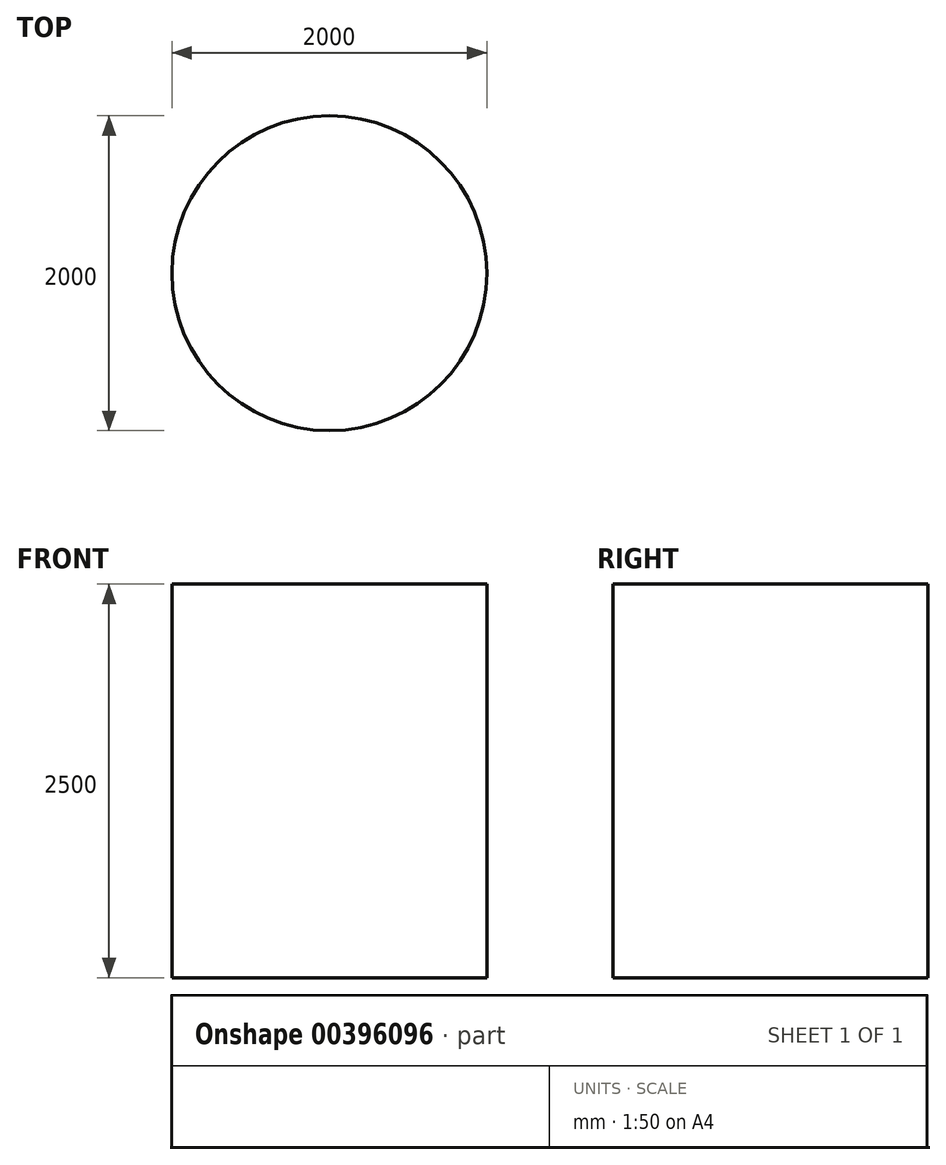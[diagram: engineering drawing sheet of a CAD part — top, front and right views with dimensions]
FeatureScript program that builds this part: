
annotation { "Feature Type Name" : "Feature", "Feature Type Description" : "" }
export const myFeature = defineFeature(function(context is Context, id is Id, definition is map)
    precondition{}
    {
        {
            var Q0;
            Q0=qCreatedBy(makeId("Top.planeOp"),FACE);
            var sketch = newSketch(context, id + "F0", { "sketchPlane" : qUnion([Q0])});
            skCircle(sketch, "E0", {"center": v(0, 0) * mm, "radius": 1000 * mm});
            skSolve(sketch);
        }
        {
            var Q0;
            Q0 = qSketchRegion(id + "F0", true);
            extrude(context, id + "F1", {"entities" : qUnion([Q0]), "depth" : 2500 * mm, "offsetDistance" : 25 * mm});
        }
    });
